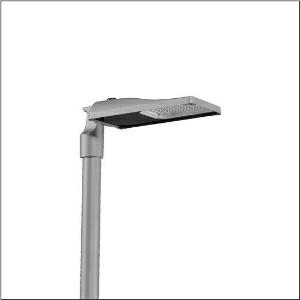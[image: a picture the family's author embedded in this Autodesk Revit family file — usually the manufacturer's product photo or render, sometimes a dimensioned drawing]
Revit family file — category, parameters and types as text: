
# Revit family: streetlight_sl_31_mini___st1_0a_5xh2d31s08ha_0250
name_source: partatom
category: Lighting Fixtures
units: mm (PartAtom-declared; Revit-internal decimal feet)

## family parameters
Cut with Voids When Loaded = No
Host = Face
Light Source = No
Part Type = Normal
Room Calculation Point = No
Round Connector Dimension = Use Diameter
Shared = No

## types (1)
- --- (1 x LED, 9230 lm, 68.3 W, 3000K)
    Apparent Load = 68 VA
    CIE Flux Codes = 37 72 97 100 100
    Color Rendering = 70
    Color Temperature = 3000K
    Default Elevation = 1800 mm
    Description = Streetlight SL 31 mini D4i, Desk-Remote mast luminaire for post-top, side-entry; light control with lens of PMMA; light distribution: ST1.0a, direct asymmetric distribution, for standard-compliant lighting for roads and squares; LED: luminous flux: 9.230lm, light colour: 730, colour temperature: 3000K; luminous efficacy: 135,3lm/W; control: pre-setting: logarithmic dimming characteristic, flexible luminous flux parameterisation, time-dependent luminous flux control, constant luminous flux control, power reduction, intelligent temperature release in ECG and LED module, overheat protection; luminaire housing, of diecast aluminium, Siteco® metallic grey (DB 702S), corrosivity category C5 high according to DIN EN ISO 12944; cover of toughened safety glass, transparent, mast flange of diecast aluminium, Siteco® metallic grey (DB 702S), spigot size: 76/60mm, mast flange included unmounted; with cable H07RN-F 2x 1.5mm², cable length: 8,5m, connection cable pre-assembled; mains connection: 220..240V, AC, 50/60Hz; power consumption (at start of service life): 68,2W / (at end of service life): 74,4W / (with reduced operation 50%): 29,7W; protection rating (complete): IP66; insulation class (complete): insulation class II (safety insulation); impact resistance: IK09; certification: CE, ENEC, ENEC+, VDE, UKCA, ZD4i; permissible operating ambient temperature for outdoor applications: -40..+50°C; packaging unit: 1 piece

Light Distribution: ST1.0a
    Height = 76 mm
    Lamp = 1 x LED
    Lamp Light Flux = 9230 lm
    Lamp Power = 68.3 W
    Lamp count = 1
    Length = 547 mm
    Luminous efficacy = 135 lm/W
    Manufacturer = Siteco
    ModVariant = No
    Model = 5XH2D31S08HA
    Number of Poles = 1
    OnlyDefault = Yes
    Power Factor = 1
    Product Name = Streetlight SL 31 mini | ST1.0a
    Product group = mast luminaire | pylon top
    ProductGroupID = 6100
    Protection Class = Protection class II
    Protection Degree = IP 66
    RLX_Detail_Level = 1
    RLX_Emergency_Light_Flux = 0 lm
    RLX_Emergency_Type = 0
    RLX_Emergency_Type_DB = No
    RlxData = <blob elided: 24169 chars, md5=91c19866>
    Socket = socket
    Standby Power = 0 W
    System Light Flux = 9230 lm
    System Power = 68 W
    Type Comments = factory setting: luminous flux: 100 % | dim-lin: 254 | 692 mA
    Type Image = l_1300330.jpg
    URL = http://relux.com
    VarID = @adj_002881
    Voltage = 0 V
    Weight = 0.00 kg
    Width = 265 mm

## geometry (parser evidence)
native form markers: Blend x4, Sweep x11
no freeform markers — native parametric forms only
